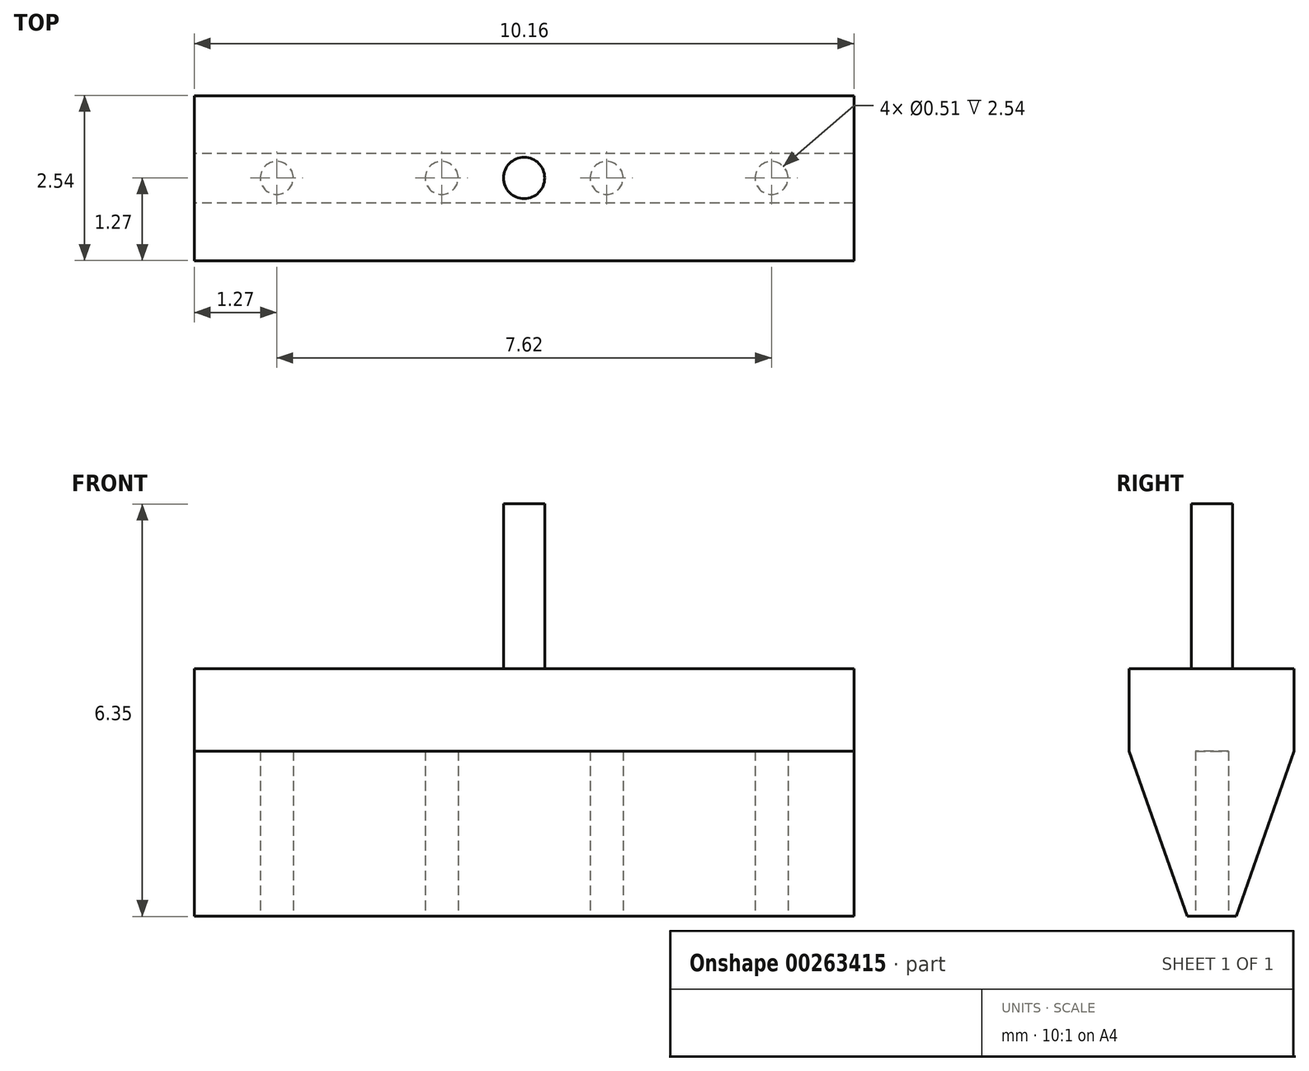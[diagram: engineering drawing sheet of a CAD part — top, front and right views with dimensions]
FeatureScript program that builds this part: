
annotation { "Feature Type Name" : "Feature", "Feature Type Description" : "" }
export const myFeature = defineFeature(function(context is Context, id is Id, definition is map)
    precondition{}
    {
        {
            var Q0;
            Q0=qCreatedBy(makeId("Right.planeOp"),FACE);
            var sketch = newSketch(context, id + "F0", { "sketchPlane" : qUnion([Q0])});
            skLineSegment(sketch, "E0.bottom", {"start": v(-1.27, 1.17) * mm, "end": v(1.27, 1.17) * mm});
            skLineSegment(sketch, "E0.top", {"start": v(-1.27, -0.1) * mm, "end": v(1.27, -0.1) * mm});
            skLineSegment(sketch, "E0.left", {"start": v(-1.27, 1.17) * mm, "end": v(-1.27, -0.1) * mm});
            skLineSegment(sketch, "E0.right", {"start": v(1.27, 1.17) * mm, "end": v(1.27, -0.1) * mm});
            skLineSegment(sketch, "E1", {"start": v(-0.38, -2.64) * mm, "end": v(-1.27, -0.1) * mm});
            skLineSegment(sketch, "E2", {"start": v(0.38, -2.64) * mm, "end": v(1.27, -0.1) * mm});
            skLineSegment(sketch, "E3", {"start": v(-0.38, -2.64) * mm, "end": v(0.38, -2.64) * mm});
            skSolve(sketch);
        }
        {
            var Q0;
            Q0=makeQuery(id+"F0.imprint","IMPRINT",FACE,{"disambiguationData":[TD([[makeQuery(id+"F0.imprint","IMPRINT",EDGE,{"derivedFrom":sQuery(id+"F0.wireOp",EDGE,"E0.bottom")}),-1.0]])]});
            var Q1;
            Q1=makeQuery(id+"F0.imprint","IMPRINT",FACE,{"disambiguationData":[TD([[makeQuery(id+"F0.imprint","IMPRINT",EDGE,{"derivedFrom":sQuery(id+"F0.wireOp",EDGE,"E0.top")}),-1.0]])]});
            extrude(context, id + "F1", {"entities" : qUnion([Q0, Q1]), "depth" : 10.16 * mm});
        }
        {
            var Q0;
            Q0=makeQuery(id+"F1.opExtrude","SWEPT_FACE",FACE,{"disambiguationData":[OSD([sQuery(id+"F0.wireOp",EDGE,"E3")])]});
            var sketch = newSketch(context, id + "F2", { "sketchPlane" : qUnion([Q0])});
            skCircle(sketch, "E4", {"center": v(8.9, 0) * mm, "radius": 0.25 * mm});
            skCircle(sketch, "E5", {"center": v(1.27, 0) * mm, "radius": 0.25 * mm});
            skCircle(sketch, "E6", {"center": v(6.35, 0) * mm, "radius": 0.25 * mm});
            skCircle(sketch, "E7", {"center": v(3.81, 0) * mm, "radius": 0.25 * mm});
            skSolve(sketch);
        }
        {
            var Q0;
            Q0=makeQuery(id+"F2.imprint","IMPRINT",FACE,{"disambiguationData":[TD([[makeQuery(id+"F2.imprint","IMPRINT",EDGE,{"derivedFrom":sQuery(id+"F2.wireOp",EDGE,"E5")}),1.0]])]});
            extrude(context, id + "F3", {"entities" : qUnion([Q0]), "operationType" : NewBodyOperationType.REMOVE, "oppositeDirection" : true, "depth" : 2.54 * mm});
        }
        {
            var Q0;
            Q0=makeQuery(id+"F1.opExtrude","SWEPT_FACE",FACE,{"disambiguationData":[OSD([sQuery(id+"F0.wireOp",EDGE,"E0.bottom")])]});
            var sketch = newSketch(context, id + "F4", { "sketchPlane" : qUnion([Q0])});
            skCircle(sketch, "E8", {"center": v(5.08, 0) * mm, "radius": 0.32 * mm});
            skSolve(sketch);
        }
        {
            var Q0;
            Q0=makeQuery(id+"F4.imprint","IMPRINT",FACE,{"disambiguationData":[TD([[makeQuery(id+"F4.imprint","IMPRINT",EDGE,{"derivedFrom":sQuery(id+"F4.wireOp",EDGE,"E8")}),1.0]])]});
            extrude(context, id + "F5", {"entities" : qUnion([Q0]), "operationType" : NewBodyOperationType.ADD, "depth" : 2.54 * mm});
        }
        {
            var Q0;
            Q0=makeQuery(id+"F1.opExtrude","SWEPT_FACE",FACE,{"disambiguationData":[OSD([sQuery(id+"F0.wireOp",EDGE,"E3")])]});
            var sketch = newSketch(context, id + "F6", { "sketchPlane" : qUnion([Q0])});
            skCircle(sketch, "E9", {"center": v(8.9, 0) * mm, "radius": 0.25 * mm});
            skSolve(sketch);
        }
        {
            var Q0;
            Q0=makeQuery(id+"F6.imprint","IMPRINT",FACE,{"disambiguationData":[TD([[makeQuery(id+"F6.imprint","IMPRINT",EDGE,{"derivedFrom":sQuery(id+"F6.wireOp",EDGE,"E9")}),1.0]])]});
            extrude(context, id + "F7", {"entities" : qUnion([Q0]), "operationType" : NewBodyOperationType.REMOVE, "oppositeDirection" : true, "depth" : 2.54 * mm});
        }
        {
            var Q0;
            Q0=makeQuery(id+"F1.opExtrude","SWEPT_FACE",FACE,{"disambiguationData":[OSD([sQuery(id+"F0.wireOp",EDGE,"E3")])]});
            var sketch = newSketch(context, id + "F8", { "sketchPlane" : qUnion([Q0])});
            skCircle(sketch, "E10", {"center": v(3.8, 0) * mm, "radius": 0.25 * mm});
            skSolve(sketch);
        }
        {
            var Q0;
            Q0=makeQuery(id+"F8.imprint","IMPRINT",FACE,{"disambiguationData":[TD([[makeQuery(id+"F8.imprint","IMPRINT",EDGE,{"derivedFrom":sQuery(id+"F8.wireOp",EDGE,"E10")}),1.0]])]});
            extrude(context, id + "F9", {"entities" : qUnion([Q0]), "operationType" : NewBodyOperationType.REMOVE, "oppositeDirection" : true, "depth" : 2.54 * mm});
        }
        {
            var Q0;
            Q0=makeQuery(id+"F1.opExtrude","SWEPT_FACE",FACE,{"disambiguationData":[OSD([sQuery(id+"F0.wireOp",EDGE,"E3")])]});
            var sketch = newSketch(context, id + "F10", { "sketchPlane" : qUnion([Q0])});
            skCircle(sketch, "E11", {"center": v(6.35, 0) * mm, "radius": 0.25 * mm});
            skSolve(sketch);
        }
        {
            var Q0;
            Q0=makeQuery(id+"F10.imprint","IMPRINT",FACE,{"disambiguationData":[TD([[makeQuery(id+"F10.imprint","IMPRINT",EDGE,{"derivedFrom":sQuery(id+"F10.wireOp",EDGE,"E11")}),1.0]])]});
            extrude(context, id + "F11", {"entities" : qUnion([Q0]), "operationType" : NewBodyOperationType.REMOVE, "oppositeDirection" : true, "depth" : 2.54 * mm});
        }
    });
